# Revit family: Basin-Wall_Hung-DXV-EQUILITY-D21415033
name_source: partatom
category: Plumbing Fixtures
revit_build: Autodesk Revit 2014 (Build: 20130308_1515(x64)
units: mm (PartAtom-declared; Revit-internal decimal feet)

## types (2) — shared parameters
Assembly Code = D2010310
Basin Shape = Rectangle Rounded Front
CW Connection = Yes
CWFU = 1.5
Cold Water Connection Diameter = 1/2"
Cold Water Connection Height = 19 3/4"
Cold Water Connection Radius = 1/4"
Cold Water Connection Width = 4"
Default Elevation = 34"
HW Connection = Yes
HWFU = 1.5
Height = 2 9/16"
Hot Water Connection Diameter = 1/2"
Hot Water Connection Height = 19 3/4"
Hot Water Connection Radius = 1/4"
Hot Water Connection Width = 4"
Installation Type = Wall-Mounted
Length = 17 11/16"
Manufacturer = DXV
Materials = Fine Fire Clay-DXV-415-Canvas White
Price = Prices may vary. Please consult Manufacturer Representative for most up-to-date price list.
Product Documentation Link = https://dxv01.blob.core.windows.net
Product Page URL = https://www.dxv.com
URL = https://www.dxv.com
Vent Connection = No
WFU = 2
Warranty Documentation Link = https://www.dxv.com
Waste Connection = Yes
Waste Connection Diameter = 1 1/4"
Waste Connection Height = 18 1/8"
Waste Connection Radius = 5/8"
Width = 32 3/4"

## per-type parameters (varying)
| type | Description | Wood Finish |
| D21415033.414 | EQUILITY™(Formerly LYNDON®) 22" WALL-HUNG VANITY conjunction with 22" Equility Lavatory (D20075001.415) Natural Oak (414) | Wood-DXV-414-Natural Oak |
| D21415033.610 | EQUILITY™(Formerly LYNDON®) 33" WALL-HUNG VANITY conjunction with 22" Equility Lavatory (D20076001.415) Wenge (610) | Wood-DXV-610-Wenge |

note: column(s) folded — value = type name in every type: Model

## geometry (parser evidence)
native form markers: Sweep x2
no freeform markers — native parametric forms only
